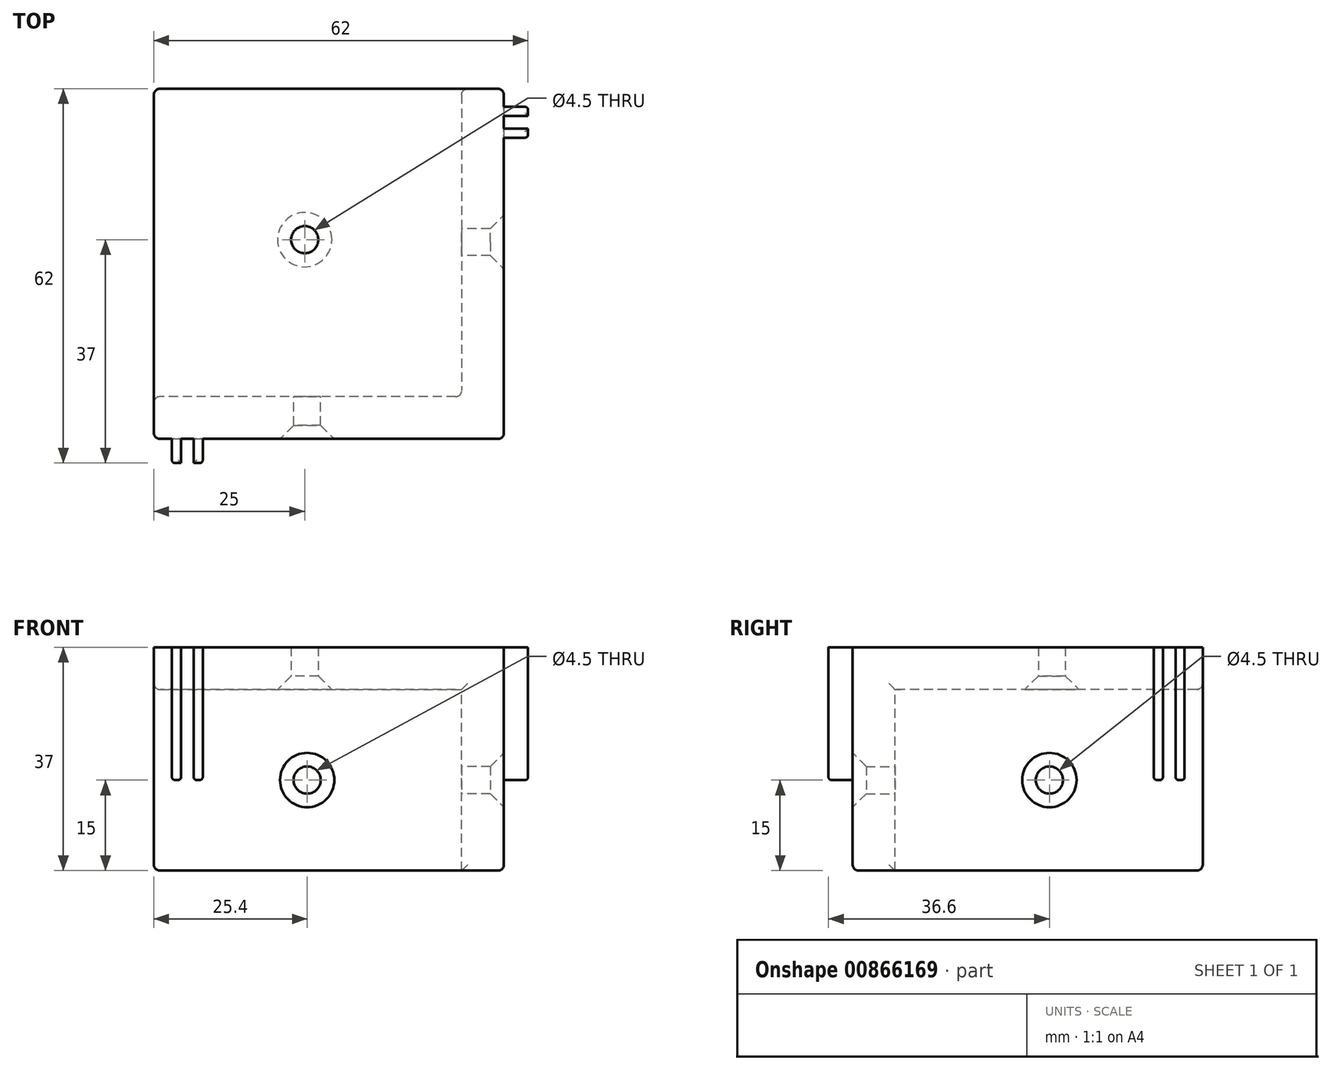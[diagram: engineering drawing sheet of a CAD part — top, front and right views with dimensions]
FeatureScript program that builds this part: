
annotation { "Feature Type Name" : "Feature", "Feature Type Description" : "" }
export const myFeature = defineFeature(function(context is Context, id is Id, definition is map)
    precondition{}
    {
        {
            var Q0;
            Q0=qCreatedBy(makeId("Top.planeOp"),FACE);
            var sketch = newSketch(context, id + "F0", { "sketchPlane" : qUnion([Q0])});
            skLineSegment(sketch, "E0.bottom", {"start": v(-58, 58) * mm, "end": v(0, 58) * mm});
            skLineSegment(sketch, "E0.top", {"start": v(-58, 0) * mm, "end": v(0, 0) * mm});
            skLineSegment(sketch, "E0.left", {"start": v(-58, 58) * mm, "end": v(-58, 0) * mm});
            skLineSegment(sketch, "E0.right", {"start": v(0, 58) * mm, "end": v(0, 0) * mm});
            skCircle(sketch, "E1", {"center": v(-33, 33) * mm, "radius": 2.25 * mm});
            skSolve(sketch);
        }
        {
            var Q0;
            Q0=makeQuery(id+"F0.imprint","IMPRINT",FACE,{"disambiguationData":[TD([[makeQuery(id+"F0.imprint","IMPRINT",EDGE,{"derivedFrom":sQuery(id+"F0.wireOp",EDGE,"E0.bottom")}),-1.0]])]});
            extrude(context, id + "F1", {"entities" : qUnion([Q0]), "depth" : 7 * mm, "offsetDistance" : 25 * mm});
        }
        {
            var Q0;
            Q0=makeQuery(id+"F1.opExtrude","CAP_FACE",FACE,{"disambiguationData":[OSD([sQuery(id+"F0.wireOp",EDGE,"E0.bottom"),sQuery(id+"F0.wireOp",EDGE,"E0.top"),sQuery(id+"F0.wireOp",EDGE,"E0.left"),sQuery(id+"F0.wireOp",EDGE,"E0.right"),sQuery(id+"F0.wireOp",EDGE,"E1")])],"isStart":true});
            var sketch = newSketch(context, id + "F2", { "sketchPlane" : qUnion([Q0])});
            skLineSegment(sketch, "E2", {"start": v(0, 0) * mm, "end": v(0, -58) * mm});
            skLineSegment(sketch, "E3", {"start": v(0, -58) * mm, "end": v(-7, -58) * mm});
            skLineSegment(sketch, "E4", {"start": v(-7, -58) * mm, "end": v(-7, -7) * mm});
            skLineSegment(sketch, "E5", {"start": v(-7, -7) * mm, "end": v(-58, -7) * mm});
            skLineSegment(sketch, "E6", {"start": v(-58, -7) * mm, "end": v(-58, 0) * mm});
            skLineSegment(sketch, "E7", {"start": v(-58, 0) * mm, "end": v(0, 0) * mm});
            skSolve(sketch);
        }
        {
            var Q0;
            Q0=makeQuery(id+"F2.imprint","IMPRINT",FACE,{"disambiguationData":[TD([[makeQuery(id+"F2.imprint","IMPRINT",EDGE,{"derivedFrom":sQuery(id+"F2.wireOp",EDGE,"E2")}),1.0]])]});
            extrude(context, id + "F3", {"entities" : qUnion([Q0]), "operationType" : NewBodyOperationType.ADD, "depth" : 30 * mm, "offsetDistance" : 25 * mm});
        }
        {
            var Q0;
            Q0=makeQuery(id+"F3.opExtrude","SWEPT_FACE",FACE,{"disambiguationData":[OSD([sQuery(id+"F2.wireOp",EDGE,"E4")])]});
            var sketch = newSketch(context, id + "F4", { "sketchPlane" : qUnion([Q0])});
            skCircle(sketch, "E8", {"center": v(-32.6, -15) * mm, "radius": 2.25 * mm});
            skSolve(sketch);
        }
        {
            var Q0;
            Q0=makeQuery(id+"F4.imprint","IMPRINT",FACE,{"disambiguationData":[TD([[makeQuery(id+"F4.imprint","IMPRINT",EDGE,{"derivedFrom":sQuery(id+"F4.wireOp",EDGE,"E8")}),1.0]])]});
            extrude(context, id + "F5", {"entities" : qUnion([Q0]), "operationType" : NewBodyOperationType.REMOVE, "oppositeDirection" : true, "depth" : 25 * mm, "offsetDistance" : 25 * mm});
        }
        {
            var Q0;
            Q0=makeQuery(id+"F3.opExtrude","SWEPT_FACE",FACE,{"disambiguationData":[OSD([sQuery(id+"F2.wireOp",EDGE,"E5")])]});
            var sketch = newSketch(context, id + "F6", { "sketchPlane" : qUnion([Q0])});
            skCircle(sketch, "E9", {"center": v(32.6, -15) * mm, "radius": 2.25 * mm});
            skSolve(sketch);
        }
        {
            var Q0;
            Q0=makeQuery(id+"F6.imprint","IMPRINT",FACE,{"disambiguationData":[TD([[makeQuery(id+"F6.imprint","IMPRINT",EDGE,{"derivedFrom":sQuery(id+"F6.wireOp",EDGE,"E9")}),1.0]])]});
            extrude(context, id + "F7", {"entities" : qUnion([Q0]), "operationType" : NewBodyOperationType.REMOVE, "oppositeDirection" : true, "depth" : 25 * mm, "offsetDistance" : 25 * mm});
        }
        {
            var Q0;
            Q0=makeQuery(id+"F3.opExtrude","CAP_EDGE",EDGE,{"disambiguationData":[OSD([sQuery(id+"F2.wireOp",EDGE,"E7")])],"isStart":false});
            fillet(context, id + "F8", {"entities" : qUnion([Q0]), "radius" : 1 * mm, "tangentPropagation" : true, "allowEdgeOverflow" : false});
        }
        {
            var Q0;
            Q0=makeQuery(id+"F3.opExtrude","CAP_EDGE",EDGE,{"disambiguationData":[OSD([sQuery(id+"F2.wireOp",EDGE,"E2")])],"isStart":false});
            fillet(context, id + "F9", {"entities" : qUnion([Q0]), "radius" : 1 * mm, "tangentPropagation" : true, "allowEdgeOverflow" : false});
        }
        {
            var Q0;
            Q0=makeQuery(id+"F3.opExtrude","CAP_EDGE",EDGE,{"disambiguationData":[OSD([sQuery(id+"F2.wireOp",EDGE,"E4")])],"isStart":true});
            var Q1;
            Q1=makeQuery(id+"F3.opExtrude","SWEPT_EDGE",EDGE,{"disambiguationData":[OSD([sQuery(id+"F2.wireOp",EDGE,"E4"),sQuery(id+"F2.wireOp",EDGE,"E5")])]});
            var Q2;
            Q2=makeQuery(id+"F3.opExtrude","CAP_EDGE",EDGE,{"disambiguationData":[OSD([sQuery(id+"F2.wireOp",EDGE,"E5")])],"isStart":true});
            fillet(context, id + "F10", {"entities" : qUnion([Q0, Q1, Q2]), "radius" : 1 * mm, "tangentPropagation" : true, "allowEdgeOverflow" : false});
        }
        {
            var Q0;
            Q0=makeQuery(id+"F3.opExtrude","CAP_EDGE",EDGE,{"disambiguationData":[OSD([sQuery(id+"F2.wireOp",EDGE,"E6")])],"isStart":false});
            var Q1;
            Q1=makeQuery(id+"F3.boolean.opBoolean","MERGE",EDGE,{"derivedFrom":[makeQuery(id+"F1.opExtrude","SWEPT_EDGE",EDGE,{"disambiguationData":[OSD([sQuery(id+"F0.wireOp",EDGE,"E0.top"),sQuery(id+"F0.wireOp",EDGE,"E0.left")])]}),makeQuery(id+"F3.opExtrude","SWEPT_EDGE",EDGE,{"disambiguationData":[OSD([sQuery(id+"F2.wireOp",EDGE,"E6"),sQuery(id+"F2.wireOp",EDGE,"E7")])]})]});
            var Q2;
            Q2=makeQuery(id+"F1.opExtrude","CAP_EDGE",EDGE,{"disambiguationData":[OSD([sQuery(id+"F0.wireOp",EDGE,"E0.left")])],"isStart":true});
            var Q3;
            Q3=makeQuery(id+"F3.opExtrude","SWEPT_EDGE",EDGE,{"disambiguationData":[OSD([sQuery(id+"F0.wireOp",EDGE,"E0.left"),sQuery(id+"F2.wireOp",EDGE,"E5"),sQuery(id+"F2.wireOp",EDGE,"E6")])]});
            var Q4;
            Q4=makeQuery(id+"F10.opFillet","BLEND_EDGE",EDGE,{"blendedFrom":[makeQuery(id+"F3.opExtrude","CAP_EDGE",EDGE,{"disambiguationData":[OSD([sQuery(id+"F2.wireOp",EDGE,"E5")])],"isStart":true}),makeQuery(id+"F3.boolean.opBoolean","MERGE",FACE,{"derivedFrom":[makeQuery(id+"F1.opExtrude","SWEPT_FACE",FACE,{"disambiguationData":[OSD([sQuery(id+"F0.wireOp",EDGE,"E0.left")])]}),makeQuery(id+"F3.opExtrude","SWEPT_FACE",FACE,{"disambiguationData":[OSD([sQuery(id+"F2.wireOp",EDGE,"E6")])]})]})],"blendedInto":[makeQuery(id+"F3.boolean.opBoolean","MERGE",FACE,{"derivedFrom":[makeQuery(id+"F1.opExtrude","SWEPT_FACE",FACE,{"disambiguationData":[OSD([sQuery(id+"F0.wireOp",EDGE,"E0.left")])]}),makeQuery(id+"F3.opExtrude","SWEPT_FACE",FACE,{"disambiguationData":[OSD([sQuery(id+"F2.wireOp",EDGE,"E6")])]})]})]});
            var Q5;
            Q5=makeQuery(id+"F8.opFillet","BLEND_EDGE",EDGE,{"blendedFrom":[makeQuery(id+"F3.opExtrude","CAP_EDGE",EDGE,{"disambiguationData":[OSD([sQuery(id+"F2.wireOp",EDGE,"E7")])],"isStart":false}),makeQuery(id+"F3.boolean.opBoolean","MERGE",FACE,{"derivedFrom":[makeQuery(id+"F1.opExtrude","SWEPT_FACE",FACE,{"disambiguationData":[OSD([sQuery(id+"F0.wireOp",EDGE,"E0.left")])]}),makeQuery(id+"F3.opExtrude","SWEPT_FACE",FACE,{"disambiguationData":[OSD([sQuery(id+"F2.wireOp",EDGE,"E6")])]})]})],"blendedInto":[makeQuery(id+"F3.boolean.opBoolean","MERGE",FACE,{"derivedFrom":[makeQuery(id+"F1.opExtrude","SWEPT_FACE",FACE,{"disambiguationData":[OSD([sQuery(id+"F0.wireOp",EDGE,"E0.left")])]}),makeQuery(id+"F3.opExtrude","SWEPT_FACE",FACE,{"disambiguationData":[OSD([sQuery(id+"F2.wireOp",EDGE,"E6")])]})]})]});
            var Q6;
            Q6=makeQuery(id+"F1.opExtrude","SWEPT_EDGE",EDGE,{"disambiguationData":[OSD([sQuery(id+"F0.wireOp",EDGE,"E0.bottom"),sQuery(id+"F0.wireOp",EDGE,"E0.left")])]});
            var Q7;
            Q7=makeQuery(id+"F1.opExtrude","CAP_EDGE",EDGE,{"disambiguationData":[OSD([sQuery(id+"F0.wireOp",EDGE,"E0.bottom")])],"isStart":true});
            var Q8;
            Q8=makeQuery(id+"F10.opFillet","BLEND_EDGE",EDGE,{"blendedFrom":[makeQuery(id+"F3.opExtrude","CAP_EDGE",EDGE,{"disambiguationData":[OSD([sQuery(id+"F2.wireOp",EDGE,"E4")])],"isStart":true}),makeQuery(id+"F3.boolean.opBoolean","MERGE",FACE,{"derivedFrom":[makeQuery(id+"F1.opExtrude","SWEPT_FACE",FACE,{"disambiguationData":[OSD([sQuery(id+"F0.wireOp",EDGE,"E0.bottom")])]}),makeQuery(id+"F3.opExtrude","SWEPT_FACE",FACE,{"disambiguationData":[OSD([sQuery(id+"F2.wireOp",EDGE,"E3")])]})]})],"blendedInto":[makeQuery(id+"F3.boolean.opBoolean","MERGE",FACE,{"derivedFrom":[makeQuery(id+"F1.opExtrude","SWEPT_FACE",FACE,{"disambiguationData":[OSD([sQuery(id+"F0.wireOp",EDGE,"E0.bottom")])]}),makeQuery(id+"F3.opExtrude","SWEPT_FACE",FACE,{"disambiguationData":[OSD([sQuery(id+"F2.wireOp",EDGE,"E3")])]})]})]});
            var Q9;
            Q9=makeQuery(id+"F3.opExtrude","CAP_EDGE",EDGE,{"disambiguationData":[OSD([sQuery(id+"F2.wireOp",EDGE,"E3")])],"isStart":false});
            var Q10;
            Q10=makeQuery(id+"F3.opExtrude","SWEPT_EDGE",EDGE,{"disambiguationData":[OSD([sQuery(id+"F0.wireOp",EDGE,"E0.bottom"),sQuery(id+"F2.wireOp",EDGE,"E3"),sQuery(id+"F2.wireOp",EDGE,"E4")])]});
            var Q11;
            Q11=makeQuery(id+"F3.boolean.opBoolean","MERGE",EDGE,{"derivedFrom":[makeQuery(id+"F1.opExtrude","SWEPT_EDGE",EDGE,{"disambiguationData":[OSD([sQuery(id+"F0.wireOp",EDGE,"E0.bottom"),sQuery(id+"F0.wireOp",EDGE,"E0.right")])]}),makeQuery(id+"F3.opExtrude","SWEPT_EDGE",EDGE,{"disambiguationData":[OSD([sQuery(id+"F2.wireOp",EDGE,"E2"),sQuery(id+"F2.wireOp",EDGE,"E3")])]})]});
            fillet(context, id + "F11", {"entities" : qUnion([Q0, Q1, Q2, Q3, Q4, Q5, Q6, Q7, Q8, Q9, Q10, Q11]), "radius" : 1 * mm, "tangentPropagation" : true, "allowEdgeOverflow" : false});
        }
        {
            var Q0;
            Q0=makeQuery(id+"F1.opExtrude","CAP_EDGE",EDGE,{"disambiguationData":[OSD([sQuery(id+"F0.wireOp",EDGE,"E1")])],"isStart":true});
            var Q1;
            Q1=makeQuery(id+"F7.boolean.opBoolean","INTERSECT",EDGE,{"derivedFrom":[makeQuery(id+"F3.boolean.opBoolean","MERGE",FACE,{"derivedFrom":[makeQuery(id+"F1.opExtrude","SWEPT_FACE",FACE,{"disambiguationData":[OSD([sQuery(id+"F0.wireOp",EDGE,"E0.top")])]}),makeQuery(id+"F3.opExtrude","SWEPT_FACE",FACE,{"disambiguationData":[OSD([sQuery(id+"F2.wireOp",EDGE,"E7")])]})]}),makeQuery(id+"F7.opExtrude","SWEPT_FACE",FACE,{"disambiguationData":[OSD([sQuery(id+"F6.wireOp",EDGE,"E9")])]})]});
            var Q2;
            Q2=makeQuery(id+"F5.boolean.opBoolean","INTERSECT",EDGE,{"derivedFrom":[makeQuery(id+"F3.boolean.opBoolean","MERGE",FACE,{"derivedFrom":[makeQuery(id+"F1.opExtrude","SWEPT_FACE",FACE,{"disambiguationData":[OSD([sQuery(id+"F0.wireOp",EDGE,"E0.right")])]}),makeQuery(id+"F3.opExtrude","SWEPT_FACE",FACE,{"disambiguationData":[OSD([sQuery(id+"F2.wireOp",EDGE,"E2")])]})]}),makeQuery(id+"F5.opExtrude","SWEPT_FACE",FACE,{"disambiguationData":[OSD([sQuery(id+"F4.wireOp",EDGE,"E8")])]})]});
            chamfer(context, id + "F12", {"entities" : qUnion([Q0, Q1, Q2]), "chamferType" : ChamferType.OFFSET_ANGLE, "width" : 2.25 * mm, "oppositeDirection" : false, "angle" : 45 * degree, "tangentPropagation" : true});
        }
        {
            var Q0;
            Q0=makeQuery(id+"F3.boolean.opBoolean","MERGE",FACE,{"derivedFrom":[makeQuery(id+"F1.opExtrude","SWEPT_FACE",FACE,{"disambiguationData":[OSD([sQuery(id+"F0.wireOp",EDGE,"E0.top")])]}),makeQuery(id+"F3.opExtrude","SWEPT_FACE",FACE,{"disambiguationData":[OSD([sQuery(id+"F2.wireOp",EDGE,"E7")])]})]});
            var sketch = newSketch(context, id + "F13", { "sketchPlane" : qUnion([Q0])});
            skLineSegment(sketch, "E10.bottom", {"start": v(-55, 7) * mm, "end": v(-53.5, 7) * mm});
            skLineSegment(sketch, "E10.top", {"start": v(-55, -15) * mm, "end": v(-53.5, -15) * mm});
            skLineSegment(sketch, "E10.left", {"start": v(-55, 7) * mm, "end": v(-55, -15) * mm});
            skLineSegment(sketch, "E10.right", {"start": v(-53.5, 7) * mm, "end": v(-53.5, -15) * mm});
            skLineSegment(sketch, "E11.bottom", {"start": v(-51.4, 7) * mm, "end": v(-49.9, 7) * mm});
            skLineSegment(sketch, "E11.top", {"start": v(-51.4, -15) * mm, "end": v(-49.9, -15) * mm});
            skLineSegment(sketch, "E11.left", {"start": v(-51.4, 7) * mm, "end": v(-51.4, -15) * mm});
            skLineSegment(sketch, "E11.right", {"start": v(-49.9, 7) * mm, "end": v(-49.9, -15) * mm});
            skSolve(sketch);
        }
        {
            var Q0;
            Q0=makeQuery(id+"F13.imprint","IMPRINT",FACE,{"disambiguationData":[TD([[makeQuery(id+"F13.imprint","IMPRINT",EDGE,{"derivedFrom":sQuery(id+"F13.wireOp",EDGE,"E11.bottom")}),-1.0]])]});
            var Q1;
            Q1=makeQuery(id+"F13.imprint","IMPRINT",FACE,{"disambiguationData":[TD([[makeQuery(id+"F13.imprint","IMPRINT",EDGE,{"derivedFrom":sQuery(id+"F13.wireOp",EDGE,"E10.bottom")}),-1.0]])]});
            extrude(context, id + "F14", {"entities" : qUnion([Q0, Q1]), "operationType" : NewBodyOperationType.ADD, "depth" : 4 * mm, "offsetDistance" : 25 * mm});
        }
        {
            var Q0;
            Q0=makeQuery(id+"F3.boolean.opBoolean","MERGE",FACE,{"derivedFrom":[makeQuery(id+"F1.opExtrude","SWEPT_FACE",FACE,{"disambiguationData":[OSD([sQuery(id+"F0.wireOp",EDGE,"E0.right")])]}),makeQuery(id+"F3.opExtrude","SWEPT_FACE",FACE,{"disambiguationData":[OSD([sQuery(id+"F2.wireOp",EDGE,"E2")])]})]});
            var sketch = newSketch(context, id + "F15", { "sketchPlane" : qUnion([Q0])});
            skLineSegment(sketch, "E12.bottom", {"start": v(55, 7) * mm, "end": v(53.5, 7) * mm});
            skLineSegment(sketch, "E12.top", {"start": v(55, -15) * mm, "end": v(53.5, -15) * mm});
            skLineSegment(sketch, "E12.left", {"start": v(55, 7) * mm, "end": v(55, -15) * mm});
            skLineSegment(sketch, "E12.right", {"start": v(53.5, 7) * mm, "end": v(53.5, -15) * mm});
            skLineSegment(sketch, "E13.bottom", {"start": v(51.4, -15) * mm, "end": v(49.9, -15) * mm});
            skLineSegment(sketch, "E13.top", {"start": v(51.4, 7) * mm, "end": v(49.9, 7) * mm});
            skLineSegment(sketch, "E13.left", {"start": v(51.4, -15) * mm, "end": v(51.4, 7) * mm});
            skLineSegment(sketch, "E13.right", {"start": v(49.9, -15) * mm, "end": v(49.9, 7) * mm});
            skSolve(sketch);
        }
        {
            var Q0;
            Q0=makeQuery(id+"F15.imprint","IMPRINT",FACE,{"disambiguationData":[TD([[makeQuery(id+"F15.imprint","IMPRINT",EDGE,{"derivedFrom":sQuery(id+"F15.wireOp",EDGE,"E12.bottom")}),1.0]])]});
            var Q1;
            Q1=makeQuery(id+"F15.imprint","IMPRINT",FACE,{"disambiguationData":[TD([[makeQuery(id+"F15.imprint","IMPRINT",EDGE,{"derivedFrom":sQuery(id+"F15.wireOp",EDGE,"E13.bottom")}),-1.0]])]});
            extrude(context, id + "F16", {"entities" : qUnion([Q0, Q1]), "operationType" : NewBodyOperationType.ADD, "depth" : 4 * mm, "offsetDistance" : 25 * mm});
        }
        {
            var Q0;
            Q0=makeQuery(id+"F16.opExtrude","CAP_EDGE",EDGE,{"disambiguationData":[OSD([sQuery(id+"F15.wireOp",EDGE,"E12.top")])],"isStart":false});
            var Q1;
            Q1=makeQuery(id+"F16.opExtrude","CAP_EDGE",EDGE,{"disambiguationData":[OSD([sQuery(id+"F15.wireOp",EDGE,"E13.bottom")])],"isStart":false});
            var Q2;
            Q2=makeQuery(id+"F16.opExtrude","SWEPT_EDGE",EDGE,{"disambiguationData":[OSD([sQuery(id+"F15.wireOp",EDGE,"E13.bottom"),sQuery(id+"F15.wireOp",EDGE,"E13.left")])]});
            var Q3;
            Q3=makeQuery(id+"F16.opExtrude","SWEPT_EDGE",EDGE,{"disambiguationData":[OSD([sQuery(id+"F15.wireOp",EDGE,"E13.bottom"),sQuery(id+"F15.wireOp",EDGE,"E13.right")])]});
            var Q4;
            Q4=makeQuery(id+"F16.opExtrude","CAP_EDGE",EDGE,{"disambiguationData":[OSD([sQuery(id+"F15.wireOp",EDGE,"E13.right")])],"isStart":false});
            var Q5;
            Q5=makeQuery(id+"F16.opExtrude","SWEPT_EDGE",EDGE,{"disambiguationData":[OSD([sQuery(id+"F15.wireOp",EDGE,"E12.top"),sQuery(id+"F15.wireOp",EDGE,"E12.right")])]});
            var Q6;
            Q6=makeQuery(id+"F16.opExtrude","SWEPT_EDGE",EDGE,{"disambiguationData":[OSD([sQuery(id+"F15.wireOp",EDGE,"E12.top"),sQuery(id+"F15.wireOp",EDGE,"E12.left")])]});
            var Q7;
            Q7=makeQuery(id+"F16.opExtrude","CAP_EDGE",EDGE,{"disambiguationData":[OSD([sQuery(id+"F15.wireOp",EDGE,"E12.left")])],"isStart":false});
            fillet(context, id + "F17", {"entities" : qUnion([Q0, Q1, Q2, Q3, Q4, Q5, Q6, Q7]), "radius" : 0.5 * mm, "tangentPropagation" : true, "allowEdgeOverflow" : false});
        }
        {
            var Q0;
            Q0=makeQuery(id+"F14.opExtrude","CAP_EDGE",EDGE,{"disambiguationData":[OSD([sQuery(id+"F13.wireOp",EDGE,"E11.top")])],"isStart":false});
            var Q1;
            Q1=makeQuery(id+"F14.opExtrude","CAP_EDGE",EDGE,{"disambiguationData":[OSD([sQuery(id+"F13.wireOp",EDGE,"E10.top")])],"isStart":false});
            var Q2;
            Q2=makeQuery(id+"F14.opExtrude","CAP_EDGE",EDGE,{"disambiguationData":[OSD([sQuery(id+"F13.wireOp",EDGE,"E11.right")])],"isStart":false});
            var Q3;
            Q3=makeQuery(id+"F14.opExtrude","SWEPT_EDGE",EDGE,{"disambiguationData":[OSD([sQuery(id+"F13.wireOp",EDGE,"E11.top"),sQuery(id+"F13.wireOp",EDGE,"E11.right")])]});
            var Q4;
            Q4=makeQuery(id+"F14.opExtrude","CAP_EDGE",EDGE,{"disambiguationData":[OSD([sQuery(id+"F13.wireOp",EDGE,"E10.left")])],"isStart":false});
            var Q5;
            Q5=makeQuery(id+"F14.opExtrude","SWEPT_EDGE",EDGE,{"disambiguationData":[OSD([sQuery(id+"F13.wireOp",EDGE,"E10.top"),sQuery(id+"F13.wireOp",EDGE,"E10.left")])]});
            var Q6;
            Q6=makeQuery(id+"F14.opExtrude","SWEPT_EDGE",EDGE,{"disambiguationData":[OSD([sQuery(id+"F13.wireOp",EDGE,"E10.top"),sQuery(id+"F13.wireOp",EDGE,"E10.right")])]});
            var Q7;
            Q7=makeQuery(id+"F14.opExtrude","SWEPT_EDGE",EDGE,{"disambiguationData":[OSD([sQuery(id+"F13.wireOp",EDGE,"E11.top"),sQuery(id+"F13.wireOp",EDGE,"E11.left")])]});
            fillet(context, id + "F18", {"entities" : qUnion([Q0, Q1, Q2, Q3, Q4, Q5, Q6, Q7]), "radius" : 0.5 * mm, "tangentPropagation" : true, "allowEdgeOverflow" : false});
        }
    });
